# Revit family: for update_72516SGP_new
name_source: partatom
category: Plumbing Fixtures
revit_build: Autodesk Revit 2018 (Build: 20170223_1515(x64)
units: mm (PartAtom-declared; Revit-internal decimal feet)

## family parameters
Always vertical = No
Cut with Voids When Loaded = No
OmniClass Number = 23.45.55.17
OmniClass Title = Mixing Faucets
Part Type = Normal
Room Calculation Point = No
Round Connector Dimension = Use Diameter
Shared = No
Work Plane-Based = Yes

## types (1)
- 009 Chrome
    Always visible = Yes
    BIMobject category = Taps & Mixers
    Cold Water Inlet = 10 mm
    Cold Water Inlet Description = Cold Water Inlet 9.5 mm
    Default Elevation = 1219.2 mm  [stored 4 ft]
    Description = Rebris S Single lever basin mixer 80 with push-open waste set 3 ticks
    Design country = Germany
    EAN code = 4059625420539
    Edition number = 1
    GTIN code = https://4059625420539
    Hot Water Inlet = 10 mm
    Hot Water Inlet Description = Hot Water Inlet 9.5 mm
    IFC Classification = Valve
    Manufacturer = Hansgrohe
    Manufacturer country = Germany
    Manufacturer name = hansgrohe
    Material 1 = Hansgrohe - Metal - 009 Chrome
    Model = 72516SGP
    OmniClass Code = 23-31 11 00
    OmniClass Description = Faucets
    Product Guid = 879f686c-5c60-4152-843b-167418226283
    Product SKU = 72516SGP
    Product data url = https://bimobject.com
    Product family = Rebris S
    Product group = Basin mixers
    Product name = 72516SGP Rebris S Single lever basin mixer 80 with push-open waste set 3 ticks
    QR code = https://bimobject.com
    UNSPSC Code = 301815
    URL = https://www.hansgrohe.com
    Weight Net (Kg) = 1.2

note: [stored X ft] marks values corroborated as IEEE doubles in the binary element streams (Revit-internal decimal feet)

## geometry (parser evidence)
native form markers: Sweep x2
no freeform markers — native parametric forms only
